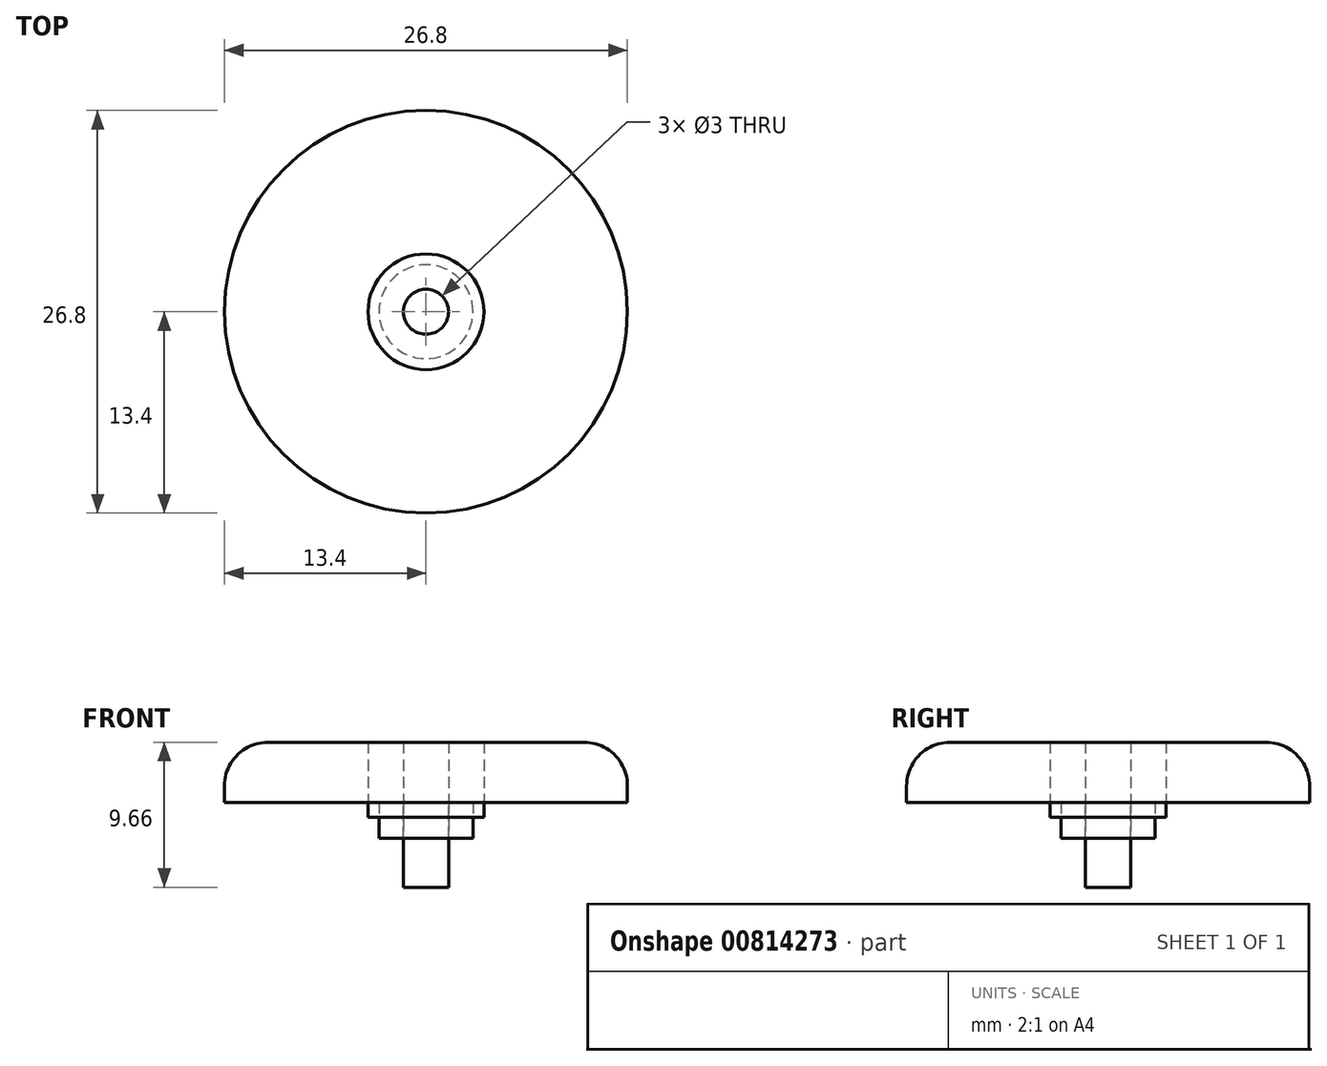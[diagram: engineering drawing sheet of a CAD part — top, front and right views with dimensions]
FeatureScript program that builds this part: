
annotation { "Feature Type Name" : "Feature", "Feature Type Description" : "" }
export const myFeature = defineFeature(function(context is Context, id is Id, definition is map)
    precondition{}
    {
        {
            var Q0;
            Q0=qCreatedBy(makeId("Top.planeOp"),FACE);
            var sketch = newSketch(context, id + "F0", { "sketchPlane" : qUnion([Q0])});
            skCircle(sketch, "E0", {"center": v(0, 0) * mm, "radius": 3.13 * mm});
            skCircle(sketch, "E1", {"center": v(0, 0) * mm, "radius": 1.5 * mm});
            skSolve(sketch);
        }
        {
            var Q0;
            Q0=makeQuery(id+"F0.imprint","IMPRINT",FACE,{"disambiguationData":[TD([[makeQuery(id+"F0.imprint","IMPRINT",EDGE,{"derivedFrom":sQuery(id+"F0.wireOp",EDGE,"E0")}),1.0]])]});
            extrude(context, id + "F1", {"entities" : qUnion([Q0]), "depth" : 2.38 * mm, "offsetDistance" : 25 * mm});
        }
        {
            var Q0;
            Q0=makeQuery(id+"F1.opExtrude","CAP_FACE",FACE,{"disambiguationData":[OSD([sQuery(id+"F0.wireOp",EDGE,"E0")])],"isStart":false});
            var sketch = newSketch(context, id + "F2", { "sketchPlane" : qUnion([Q0])});
            skCircle(sketch, "E2", {"center": v(0, 0) * mm, "radius": 13.4 * mm});
            skCircle(sketch, "E3", {"center": v(0, 0) * mm, "radius": 1.5 * mm});
            skSolve(sketch);
        }
        {
            var Q0;
            Q0=makeQuery(id+"F2.imprint","IMPRINT",FACE,{"disambiguationData":[TD([[makeQuery(id+"F2.imprint","IMPRINT",EDGE,{"derivedFrom":sQuery(id+"F2.wireOp",EDGE,"E2")}),1.0]])]});
            var Q1;
            Q1=makeQuery(id+"F2.imprint","IMPRINT",FACE,{"disambiguationData":[TD([[makeQuery(id+"F2.imprint","IMPRINT",EDGE,{"derivedFrom":makeQuery(id+"F1.opExtrude","CAP_EDGE",EDGE,{"disambiguationData":[OSD([sQuery(id+"F0.wireOp",EDGE,"E0")])],"isStart":false})}),1.0]])]});
            extrude(context, id + "F3", {"entities" : qUnion([Q0, Q1]), "depth" : 4 * mm, "offsetDistance" : 25 * mm});
        }
        {
            var Q0;
            Q0=makeQuery(id+"F3.opExtrude","CAP_EDGE",EDGE,{"disambiguationData":[OSD([sQuery(id+"F2.wireOp",EDGE,"E2")])],"isStart":false});
            fillet(context, id + "F4", {"entities" : qUnion([Q0]), "radius" : 2.9 * mm, "tangentPropagation" : true, "allowEdgeOverflow" : false});
        }
        {
            var Q0;
            Q0=makeQuery(id+"F3.opExtrude","CAP_FACE",FACE,{"disambiguationData":[OSD([sQuery(id+"F2.wireOp",EDGE,"E2")])],"isStart":true});
            var sketch = newSketch(context, id + "F5", { "sketchPlane" : qUnion([Q0])});
            skCircle(sketch, "E4", {"center": v(0, 0) * mm, "radius": 3.85 * mm});
            skSolve(sketch);
        }
        {
            var Q0;
            Q0=makeQuery(id+"F5.imprint","IMPRINT",FACE,{"disambiguationData":[TD([[makeQuery(id+"F5.imprint","IMPRINT",EDGE,{"derivedFrom":sQuery(id+"F5.wireOp",EDGE,"E4")}),1.0]])]});
            extrude(context, id + "F6", {"entities" : qUnion([Q0]), "depth" : 1 * mm, "offsetDistance" : 25 * mm});
        }
        {
            var Q0;
            Q0 = qSketchRegion(id + "F5", true);
            extrude(context, id + "F7", {"entities" : qUnion([Q0]), "oppositeDirection" : true, "depth" : 4 * mm, "offsetDistance" : 25 * mm});
        }
        {
            var Q0;
            Q0=makeQuery(id+"F2.imprint","IMPRINT",FACE,{"disambiguationData":[TD([[makeQuery(id+"F2.imprint","IMPRINT",EDGE,{"derivedFrom":sQuery(id+"F2.wireOp",EDGE,"E3")}),1.0]])]});
            extrude(context, id + "F8", {"entities" : qUnion([Q0]), "oppositeDirection" : true, "depth" : 2.37 * mm, "offsetDistance" : 25 * mm});
        }
        {
            var Q0;
            Q0=makeQuery(id+"F0.imprint","IMPRINT",FACE,{"disambiguationData":[TD([[makeQuery(id+"F0.imprint","IMPRINT",EDGE,{"derivedFrom":sQuery(id+"F0.wireOp",EDGE,"E1")}),1.0]])]});
            extrude(context, id + "F9", {"entities" : qUnion([Q0]), "oppositeDirection" : true, "depth" : 3.27 * mm, "offsetDistance" : 25 * mm});
        }
    });
